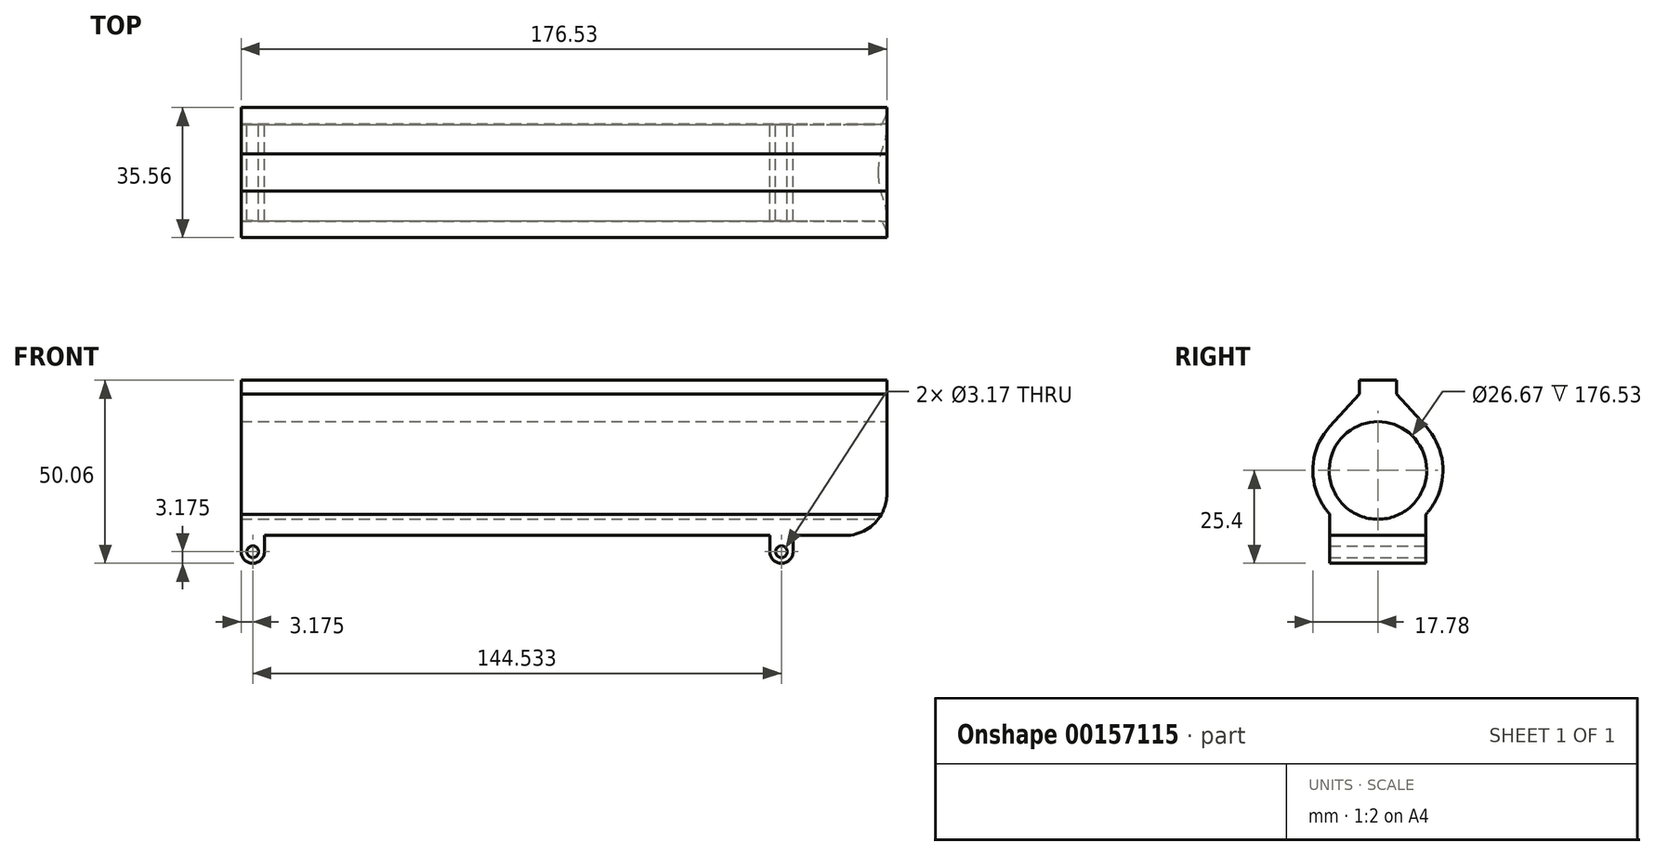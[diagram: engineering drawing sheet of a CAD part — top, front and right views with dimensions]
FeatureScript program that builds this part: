
annotation { "Feature Type Name" : "Feature", "Feature Type Description" : "" }
export const myFeature = defineFeature(function(context is Context, id is Id, definition is map)
    precondition{}
    {
        {
            var Q0;
            Q0=qCreatedBy(makeId("Right.planeOp"),FACE);
            var sketch = newSketch(context, id + "F0", { "sketchPlane" : qUnion([Q0])});
            skCircle(sketch, "E0", {"center": v(0, 0) * mm, "radius": 17.78 * mm});
            skSolve(sketch);
        }
        {
            var Q0;
            Q0 = qSketchRegion(id + "F0", true);
            extrude(context, id + "F1", {"entities" : qUnion([Q0]), "depth" : 165.1 * mm});
        }
        {
            var Q0;
            Q0=makeQuery(id+"F1.opExtrude","CAP_FACE",FACE,{"disambiguationData":[OSD([sQuery(id+"F0.wireOp",EDGE,"E0")])],"isStart":false});
            var sketch = newSketch(context, id + "F2", { "sketchPlane" : qUnion([Q0])});
            skLineSegment(sketch, "E1.bottom", {"start": v(-5.08, 17.04) * mm, "end": v(5.08, 17.04) * mm});
            skLineSegment(sketch, "E1.top", {"start": v(-5.08, 24.66) * mm, "end": v(5.08, 24.66) * mm});
            skLineSegment(sketch, "E1.left", {"start": v(-5.08, 17.04) * mm, "end": v(-5.08, 24.66) * mm});
            skLineSegment(sketch, "E1.right", {"start": v(5.08, 17.04) * mm, "end": v(5.08, 24.66) * mm});
            skSolve(sketch);
        }
        {
            var Q0;
            Q0 = qSketchRegion(id + "F2", true);
            var Q1;
            Q1=qCreatedBy(makeId("Right.planeOp"),FACE);
            extrude(context, id + "F3", {"entities" : qUnion([Q0]), "operationType" : NewBodyOperationType.ADD, "endBound" : BoundingType.UP_TO_SURFACE, "oppositeDirection" : true, "endBoundEntityFace" : qUnion([Q1]), "depth" : 25.4 * mm});
        }
        {
            var Q0;
            Q0=makeQuery(id+"F3.boolean.opBoolean","MERGE",FACE,{"derivedFrom":[makeQuery(id+"F1.opExtrude","CAP_FACE",FACE,{"disambiguationData":[OSD([sQuery(id+"F0.wireOp",EDGE,"E0")])],"isStart":false}),makeQuery(id+"F3.opExtrude","CAP_FACE",FACE,{"disambiguationData":[OSD([sQuery(id+"F2.wireOp",EDGE,"E1.bottom"),sQuery(id+"F2.wireOp",EDGE,"E1.top"),sQuery(id+"F2.wireOp",EDGE,"E1.left"),sQuery(id+"F2.wireOp",EDGE,"E1.right")])],"isStart":true})]});
            var sketch = newSketch(context, id + "F4", { "sketchPlane" : qUnion([Q0])});
            skLineSegment(sketch, "E2", {"start": v(-13.15, -11.97) * mm, "end": v(-13.15, -17.78) * mm});
            skPoint(sketch, "E2.endSnap0", {"position": v(0, -17.78) * mm});
            skLineSegment(sketch, "E3", {"start": v(-13.15, -17.78) * mm, "end": v(13.15, -17.78) * mm});
            skLineSegment(sketch, "E4", {"start": v(13.15, -17.78) * mm, "end": v(13.15, -11.97) * mm});
            skArc(sketch, "E5.0", {"start": v(-13.15, -11.97) * mm, "mid": v(0, -17.78) * mm, "end": v(13.15, -11.97) * mm});
            skPoint(sketch, "E6.orphan", {"position": v(-5.08, 17.04) * mm});
            skPoint(sketch, "E7.orphan", {"position": v(5.08, 17.04) * mm});
            skSolve(sketch);
        }
        {
            var Q0;
            {var subQ0=sQuery(id+"F4.wireOp",EDGE,"E4");Q0=makeQuery(id+"F4.imprint","IMPRINT",FACE,{"disambiguationData":[TD([[makeQuery(id+"F4.imprint","IMPRINT",EDGE,{"derivedFrom":subQ0}),1.0]])]});}
            var Q1;
            {var subQ0=sQuery(id+"F4.wireOp",EDGE,"E2");Q1=makeQuery(id+"F4.imprint","IMPRINT",FACE,{"disambiguationData":[TD([[makeQuery(id+"F4.imprint","IMPRINT",EDGE,{"derivedFrom":subQ0}),1.0]])]});}
            var Q2;
            Q2=makeQuery(id+"F3.boolean.opBoolean","MERGE",FACE,{"derivedFrom":[makeQuery(id+"F1.opExtrude","CAP_FACE",FACE,{"disambiguationData":[OSD([sQuery(id+"F0.wireOp",EDGE,"E0")])],"isStart":true}),makeQuery(id+"F3.opExtrude","CAP_FACE",FACE,{"disambiguationData":[OSD([dummyQuery(id+"Right.planeOp",FACE)])],"isStart":false})]});
            extrude(context, id + "F5", {"entities" : qUnion([Q0, Q1]), "operationType" : NewBodyOperationType.ADD, "endBound" : BoundingType.UP_TO_SURFACE, "oppositeDirection" : true, "endBoundEntityFace" : qUnion([Q2]), "depth" : 25.4 * mm});
        }
        {
            var Q0;
            {var subQ0=sQuery(id+"F4.wireOp",EDGE,"E5.0");var subQ1=sQuery(id+"F4.wireOp",EDGE,"E3");Q0=makeQuery(id+"F5.boolean.opBoolean","MERGE",FACE,{"derivedFrom":[makeQuery(id+"F3.boolean.opBoolean","MERGE",FACE,{"derivedFrom":[makeQuery(id+"F1.opExtrude","CAP_FACE",FACE,{"disambiguationData":[OSD([sQuery(id+"F0.wireOp",EDGE,"E0")])],"isStart":false}),makeQuery(id+"F3.opExtrude","CAP_FACE",FACE,{"disambiguationData":[OSD([sQuery(id+"F2.wireOp",EDGE,"E1.bottom"),sQuery(id+"F2.wireOp",EDGE,"E1.top"),sQuery(id+"F2.wireOp",EDGE,"E1.left"),sQuery(id+"F2.wireOp",EDGE,"E1.right")])],"isStart":true})]}),makeQuery(id+"F5.opExtrude","CAP_FACE",FACE,{"disambiguationData":[OSD([sQuery(id+"F4.wireOp",EDGE,"E2"),subQ1,subQ0])],"isStart":true}),makeQuery(id+"F5.opExtrude","CAP_FACE",FACE,{"disambiguationData":[OSD([subQ1,sQuery(id+"F4.wireOp",EDGE,"E4"),subQ0])],"isStart":true})]});}
            var sketch = newSketch(context, id + "F6", { "sketchPlane" : qUnion([Q0])});
            skCircle(sketch, "E8", {"center": v(0, 0) * mm, "radius": 13.33 * mm});
            skSolve(sketch);
        }
        {
            var Q0;
            Q0=makeQuery(id+"F6.imprint","IMPRINT",FACE,{"disambiguationData":[TD([[makeQuery(id+"F6.imprint","IMPRINT",EDGE,{"derivedFrom":sQuery(id+"F6.wireOp",EDGE,"E8")}),1.0]])]});
            extrude(context, id + "F7", {"entities" : qUnion([Q0]), "operationType" : NewBodyOperationType.REMOVE, "endBound" : BoundingType.THROUGH_ALL, "oppositeDirection" : true, "depth" : 25.4 * mm});
        }
        {
            var Q0;
            {var subQ0=sQuery(id+"F4.wireOp",EDGE,"E5.0");var subQ1=sQuery(id+"F4.wireOp",EDGE,"E3");Q0=makeQuery(id+"F5.boolean.opBoolean","MERGE",FACE,{"derivedFrom":[makeQuery(id+"F3.boolean.opBoolean","MERGE",FACE,{"derivedFrom":[makeQuery(id+"F1.opExtrude","CAP_FACE",FACE,{"disambiguationData":[OSD([sQuery(id+"F0.wireOp",EDGE,"E0")])],"isStart":false}),makeQuery(id+"F3.opExtrude","CAP_FACE",FACE,{"disambiguationData":[OSD([sQuery(id+"F2.wireOp",EDGE,"E1.bottom"),sQuery(id+"F2.wireOp",EDGE,"E1.top"),sQuery(id+"F2.wireOp",EDGE,"E1.left"),sQuery(id+"F2.wireOp",EDGE,"E1.right")])],"isStart":true})]}),makeQuery(id+"F5.opExtrude","CAP_FACE",FACE,{"disambiguationData":[OSD([sQuery(id+"F4.wireOp",EDGE,"E2"),subQ1,subQ0])],"isStart":true}),makeQuery(id+"F5.opExtrude","CAP_FACE",FACE,{"disambiguationData":[OSD([subQ1,sQuery(id+"F4.wireOp",EDGE,"E4"),subQ0])],"isStart":true})]});}
            var sketch = newSketch(context, id + "F8", { "sketchPlane" : qUnion([Q0])});
            skLineSegment(sketch, "E9", {"start": v(5.08, 20.85) * mm, "end": v(13.16, 11.96) * mm});
            skLineSegment(sketch, "E10", {"start": v(-5.08, 20.85) * mm, "end": v(-13.16, 11.96) * mm});
            skArc(sketch, "E11.0", {"start": v(-5.08, 17.04) * mm, "mid": v(-9.47, 15.05) * mm, "end": v(-13.16, 11.96) * mm});
            skLineSegment(sketch, "E12.0", {"start": v(-5.08, 17.04) * mm, "end": v(-5.08, 20.85) * mm});
            skPoint(sketch, "E13.0", {"position": v(5.08, 17.04) * mm});
            skLineSegment(sketch, "E14.0", {"start": v(5.08, 17.04) * mm, "end": v(5.08, 20.85) * mm});
            skArc(sketch, "E15.0", {"start": v(13.16, 11.96) * mm, "mid": v(9.47, 15.05) * mm, "end": v(5.08, 17.04) * mm});
            skPoint(sketch, "E16.orphan", {"position": v(-5.08, 24.66) * mm});
            skPoint(sketch, "E17.orphan", {"position": v(5.08, 24.66) * mm});
            skPoint(sketch, "E18.orphan", {"position": v(13.15, -11.97) * mm});
            skPoint(sketch, "E19.orphan", {"position": v(-13.15, -11.97) * mm});
            skSolve(sketch);
        }
        {
            var Q0;
            Q0=makeQuery(id+"F8.imprint","IMPRINT",FACE,{"disambiguationData":[TD([[makeQuery(id+"F8.imprint","IMPRINT",EDGE,{"derivedFrom":sQuery(id+"F8.wireOp",EDGE,"E9")}),-1.0]])]});
            var Q1;
            Q1=makeQuery(id+"F8.imprint","IMPRINT",FACE,{"disambiguationData":[TD([[makeQuery(id+"F8.imprint","IMPRINT",EDGE,{"derivedFrom":sQuery(id+"F8.wireOp",EDGE,"E10")}),1.0]])]});
            var Q2;
            {var subQ0=sQuery(id+"F4.wireOp",EDGE,"E5.0");var subQ1=sQuery(id+"F4.wireOp",EDGE,"E3");var subQ2=sQuery(id+"F0.wireOp",EDGE,"E0");var subQ3=dummyQuery(id+"Right.planeOp",FACE);Q2=makeQuery(id+"F5.boolean.opBoolean","MERGE",FACE,{"derivedFrom":[makeQuery(id+"F3.boolean.opBoolean","MERGE",FACE,{"derivedFrom":[makeQuery(id+"F1.opExtrude","CAP_FACE",FACE,{"disambiguationData":[OSD([subQ2])],"isStart":true}),makeQuery(id+"F3.opExtrude","CAP_FACE",FACE,{"disambiguationData":[OSD([subQ3])],"isStart":false})]}),makeQuery(id+"F5.opExtrude","CAP_FACE",FACE,{"disambiguationData":[OSD([subQ3,subQ2]),ownerDisambiguation([makeQuery(id+"F5.opExtrude","SWEPT_BODY",BODY,{"disambiguationData":[OSD([sQuery(id+"F4.wireOp",EDGE,"E2"),subQ1,subQ0])]})])],"isStart":false}),makeQuery(id+"F5.opExtrude","CAP_FACE",FACE,{"disambiguationData":[OSD([subQ3,subQ2]),ownerDisambiguation([makeQuery(id+"F5.opExtrude","SWEPT_BODY",BODY,{"disambiguationData":[OSD([subQ1,sQuery(id+"F4.wireOp",EDGE,"E4"),subQ0])]})])],"isStart":false})]});}
            extrude(context, id + "F9", {"entities" : qUnion([Q0, Q1]), "operationType" : NewBodyOperationType.ADD, "endBound" : BoundingType.UP_TO_SURFACE, "oppositeDirection" : true, "endBoundEntityFace" : qUnion([Q2]), "depth" : 25.4 * mm});
        }
        {
            var Q0;
            Q0=qCreatedBy(makeId("Front.planeOp"),FACE);
            var sketch = newSketch(context, id + "F10", { "sketchPlane" : qUnion([Q0])});
            skLineSegment(sketch, "E20.0", {"start": v(165.1, 20.85) * mm, "end": v(165.1, 11.96) * mm});
            skLineSegment(sketch, "E21.0", {"start": v(165.1, 20.85) * mm, "end": v(165.1, 24.66) * mm});
            skLineSegment(sketch, "E22.0", {"start": v(165.1, 11.96) * mm, "end": v(165.1, -11.97) * mm});
            skLineSegment(sketch, "E23.0", {"start": v(165.1, -11.97) * mm, "end": v(165.1, -17.78) * mm});
            skArc(sketch, "E24", {"start": v(165.1, -17.78) * mm, "mid": v(173.18, -14.43) * mm, "end": v(176.53, -6.35) * mm});
            skLineSegment(sketch, "E25", {"start": v(165.1, -17.78) * mm, "end": v(156.83, -17.78) * mm});
            skLineSegment(sketch, "E26", {"start": v(176.53, -6.35) * mm, "end": v(176.53, 24.77) * mm});
            skLineSegment(sketch, "E27", {"start": v(165.1, 24.66) * mm, "end": v(176.53, 24.77) * mm});
            skSolve(sketch);
        }
        {
            var Q0;
            Q0=sQuery(id+"F10.wireOp",EDGE,"E26");
            cPlane(context, id + "F11", {"entities" : qUnion([Q0]), "cplaneType" : CPlaneType.LINE_ANGLE, "offset" : 0 * mm, "angle" : 0 * degree, "width" : 152.4 * mm, "height" : 152.4 * mm});
        }
        {
            var Q0;
            Q0=qCreatedBy(id+"F11.planeOp",FACE);
            var sketch = newSketch(context, id + "F12", { "sketchPlane" : qUnion([Q0])});
            skLineSegment(sketch, "E28.0", {"start": v(-5.08, 20.85) * mm, "end": v(-13.16, 11.96) * mm});
            skLineSegment(sketch, "E29.0", {"start": v(-5.08, 20.85) * mm, "end": v(-5.08, 24.66) * mm});
            skLineSegment(sketch, "E30.0", {"start": v(-5.08, 24.66) * mm, "end": v(5.08, 24.66) * mm});
            skLineSegment(sketch, "E31.0", {"start": v(5.08, 20.85) * mm, "end": v(5.08, 24.66) * mm});
            skLineSegment(sketch, "E32.0", {"start": v(5.08, 20.85) * mm, "end": v(13.16, 11.96) * mm});
            skArc(sketch, "E33.0", {"start": v(13.15, -11.97) * mm, "mid": v(17.78, 0) * mm, "end": v(13.16, 11.96) * mm});
            skLineSegment(sketch, "E34.0", {"start": v(13.15, -17.78) * mm, "end": v(13.15, -11.97) * mm});
            skLineSegment(sketch, "E35.0", {"start": v(-13.15, -17.78) * mm, "end": v(13.15, -17.78) * mm});
            skLineSegment(sketch, "E36.0", {"start": v(-13.15, -11.97) * mm, "end": v(-13.15, -17.78) * mm});
            skArc(sketch, "E37.0", {"start": v(-13.16, 11.96) * mm, "mid": v(-17.78, 0) * mm, "end": v(-13.15, -11.97) * mm});
            skCircle(sketch, "E38.0", {"center": v(0, 0) * mm, "radius": 13.33 * mm});
            skSolve(sketch);
        }
        {
            var Q0;
            Q0=makeQuery(id+"F12.imprint","IMPRINT",FACE,{"disambiguationData":[TD([[makeQuery(id+"F12.imprint","IMPRINT",EDGE,{"derivedFrom":sQuery(id+"F12.wireOp",EDGE,"E28.0")}),1.0]])]});
            var Q1;
            {var subQ0=sQuery(id+"F4.wireOp",EDGE,"E5.0");var subQ1=sQuery(id+"F4.wireOp",EDGE,"E3");Q1=makeQuery(id+"F9.boolean.opBoolean","MERGE",FACE,{"derivedFrom":[makeQuery(id+"F5.boolean.opBoolean","MERGE",FACE,{"derivedFrom":[makeQuery(id+"F3.boolean.opBoolean","MERGE",FACE,{"derivedFrom":[makeQuery(id+"F1.opExtrude","CAP_FACE",FACE,{"disambiguationData":[OSD([sQuery(id+"F0.wireOp",EDGE,"E0")])],"isStart":false}),makeQuery(id+"F3.opExtrude","CAP_FACE",FACE,{"disambiguationData":[OSD([sQuery(id+"F2.wireOp",EDGE,"E1.bottom"),sQuery(id+"F2.wireOp",EDGE,"E1.top"),sQuery(id+"F2.wireOp",EDGE,"E1.left"),sQuery(id+"F2.wireOp",EDGE,"E1.right")])],"isStart":true})]}),makeQuery(id+"F5.opExtrude","CAP_FACE",FACE,{"disambiguationData":[OSD([sQuery(id+"F4.wireOp",EDGE,"E2"),subQ1,subQ0])],"isStart":true}),makeQuery(id+"F5.opExtrude","CAP_FACE",FACE,{"disambiguationData":[OSD([subQ1,sQuery(id+"F4.wireOp",EDGE,"E4"),subQ0])],"isStart":true})]}),makeQuery(id+"F9.opExtrude","CAP_FACE",FACE,{"disambiguationData":[OSD([sQuery(id+"F8.wireOp",EDGE,"E9"),sQuery(id+"F8.wireOp",EDGE,"E14.0"),sQuery(id+"F8.wireOp",EDGE,"E15.0")])],"isStart":true}),makeQuery(id+"F9.opExtrude","CAP_FACE",FACE,{"disambiguationData":[OSD([sQuery(id+"F8.wireOp",EDGE,"E10"),sQuery(id+"F8.wireOp",EDGE,"E11.0"),sQuery(id+"F8.wireOp",EDGE,"E12.0")])],"isStart":true})]});}
            extrude(context, id + "F13", {"entities" : qUnion([Q0]), "operationType" : NewBodyOperationType.ADD, "endBound" : BoundingType.UP_TO_SURFACE, "oppositeDirection" : true, "endBoundEntityFace" : qUnion([Q1]), "depth" : 25.4 * mm});
        }
        {
            var Q0;
            Q0=qCreatedBy(makeId("Front.planeOp"),FACE);
            var sketch = newSketch(context, id + "F14", { "sketchPlane" : qUnion([Q0])});
            skArc(sketch, "E39.0", {"start": v(165.1, -17.78) * mm, "mid": v(173.18, -14.43) * mm, "end": v(176.53, -6.35) * mm});
            skLineSegment(sketch, "E40.0", {"start": v(165.1, -17.78) * mm, "end": v(176.53, -17.78) * mm});
            skLineSegment(sketch, "E41.0", {"start": v(176.53, -11.97) * mm, "end": v(176.53, -17.78) * mm});
            skLineSegment(sketch, "E42.0", {"start": v(176.53, -6.35) * mm, "end": v(176.53, -11.97) * mm});
            skPoint(sketch, "E43.orphan", {"position": v(0, -17.78) * mm});
            skPoint(sketch, "E44.orphan", {"position": v(176.53, 11.96) * mm});
            skSolve(sketch);
        }
        {
            var Q0;
            Q0 = qSketchRegion(id + "F14", true);
            extrude(context, id + "F15", {"entities" : qUnion([Q0]), "operationType" : NewBodyOperationType.REMOVE, "endBound" : BoundingType.THROUGH_ALL, "oppositeDirection" : true, "depth" : 25.4 * mm, "hasSecondDirection" : true, "secondDirectionBound" : SecondDirectionBoundingType.THROUGH_ALL, "secondDirectionOppositeDirection" : false, "secondDirectionDepth" : 25.4 * mm});
        }
        {
            var Q0;
            Q0=qCreatedBy(makeId("Front.planeOp"),FACE);
            var sketch = newSketch(context, id + "F16", { "sketchPlane" : qUnion([Q0])});
            skLineSegment(sketch, "E45.bottom", {"start": v(0, -17.78) * mm, "end": v(6.35, -17.78) * mm});
            skLineSegment(sketch, "E45.left", {"start": v(0, -17.78) * mm, "end": v(0, -22.23) * mm});
            skLineSegment(sketch, "E45.right", {"start": v(6.35, -17.78) * mm, "end": v(6.35, -22.23) * mm});
            skArc(sketch, "E46", {"start": v(0, -22.23) * mm, "mid": v(3.18, -25.4) * mm, "end": v(6.35, -22.23) * mm});
            skCircle(sketch, "E47", {"center": v(3.18, -22.23) * mm, "radius": 1.59 * mm});
            skSolve(sketch);
        }
        {
            var Q0;
            Q0 = qSketchRegion(id + "F16", true);
            var Q1;
            Q1=makeQuery(id+"F13.boolean.opBoolean","MERGE",FACE,{"derivedFrom":[makeQuery(id+"F5.opExtrude","SWEPT_FACE",FACE,{"disambiguationData":[OSD([sQuery(id+"F4.wireOp",EDGE,"E2")])]}),makeQuery(id+"F13.opExtrude","SWEPT_FACE",FACE,{"disambiguationData":[OSD([sQuery(id+"F12.wireOp",EDGE,"E36.0")])]})]});
            var Q2;
            Q2=makeQuery(id+"F13.boolean.opBoolean","MERGE",FACE,{"derivedFrom":[makeQuery(id+"F5.opExtrude","SWEPT_FACE",FACE,{"disambiguationData":[OSD([sQuery(id+"F4.wireOp",EDGE,"E4")])]}),makeQuery(id+"F13.opExtrude","SWEPT_FACE",FACE,{"disambiguationData":[OSD([sQuery(id+"F12.wireOp",EDGE,"E34.0")])]})]});
            extrude(context, id + "F17", {"entities" : qUnion([Q0]), "operationType" : NewBodyOperationType.ADD, "endBound" : BoundingType.UP_TO_SURFACE, "endBoundEntityFace" : qUnion([Q1]), "depth" : 25.4 * mm, "hasSecondDirection" : true, "secondDirectionBound" : SecondDirectionBoundingType.UP_TO_SURFACE, "secondDirectionOppositeDirection" : true, "secondDirectionBoundEntityFace" : qUnion([Q2]), "secondDirectionDepth" : 25.4 * mm});
        }
        {
            var Q0;
            Q0=qCreatedBy(makeId("Front.planeOp"),FACE);
            var sketch = newSketch(context, id + "F18", { "sketchPlane" : qUnion([Q0])});
            skLineSegment(sketch, "E48.bottom", {"start": v(144.53, -17.78) * mm, "end": v(150.88, -17.78) * mm});
            skLineSegment(sketch, "E48.left", {"start": v(144.53, -17.78) * mm, "end": v(144.53, -22.23) * mm});
            skLineSegment(sketch, "E48.right", {"start": v(150.88, -17.78) * mm, "end": v(150.88, -22.23) * mm});
            skArc(sketch, "E49", {"start": v(144.53, -22.23) * mm, "mid": v(147.7, -25.4) * mm, "end": v(150.88, -22.23) * mm});
            skCircle(sketch, "E50", {"center": v(147.7, -22.23) * mm, "radius": 1.59 * mm});
            skSolve(sketch);
        }
        {
            var Q0;
            Q0 = qSketchRegion(id + "F18", true);
            var Q1;
            {var subQ0=sQuery(id+"F12.wireOp",EDGE,"E36.0");var subQ1=sQuery(id+"F4.wireOp",EDGE,"E2");Q1=makeQuery(id+"F17.boolean.opBoolean","MERGE",FACE,{"derivedFrom":[makeQuery(id+"F13.boolean.opBoolean","MERGE",FACE,{"derivedFrom":[makeQuery(id+"F5.opExtrude","SWEPT_FACE",FACE,{"disambiguationData":[OSD([subQ1])]}),makeQuery(id+"F13.opExtrude","SWEPT_FACE",FACE,{"disambiguationData":[OSD([subQ0])]})]}),makeQuery(id+"F17.opExtrude","CAP_FACE",FACE,{"disambiguationData":[OSD([subQ1,subQ0])],"isStart":false})]});}
            var Q2;
            {var subQ0=sQuery(id+"F12.wireOp",EDGE,"E34.0");var subQ1=sQuery(id+"F4.wireOp",EDGE,"E4");Q2=makeQuery(id+"F17.boolean.opBoolean","MERGE",FACE,{"derivedFrom":[makeQuery(id+"F13.boolean.opBoolean","MERGE",FACE,{"derivedFrom":[makeQuery(id+"F5.opExtrude","SWEPT_FACE",FACE,{"disambiguationData":[OSD([subQ1])]}),makeQuery(id+"F13.opExtrude","SWEPT_FACE",FACE,{"disambiguationData":[OSD([subQ0])]})]}),makeQuery(id+"F17.opExtrude","CAP_FACE",FACE,{"disambiguationData":[OSD([subQ1,subQ0])],"isStart":true})]});}
            extrude(context, id + "F19", {"entities" : qUnion([Q0]), "operationType" : NewBodyOperationType.ADD, "endBound" : BoundingType.UP_TO_SURFACE, "endBoundEntityFace" : qUnion([Q1]), "depth" : 25.4 * mm, "hasSecondDirection" : true, "secondDirectionBound" : SecondDirectionBoundingType.UP_TO_SURFACE, "secondDirectionOppositeDirection" : true, "secondDirectionBoundEntityFace" : qUnion([Q2]), "secondDirectionDepth" : 25.4 * mm});
        }
    });
